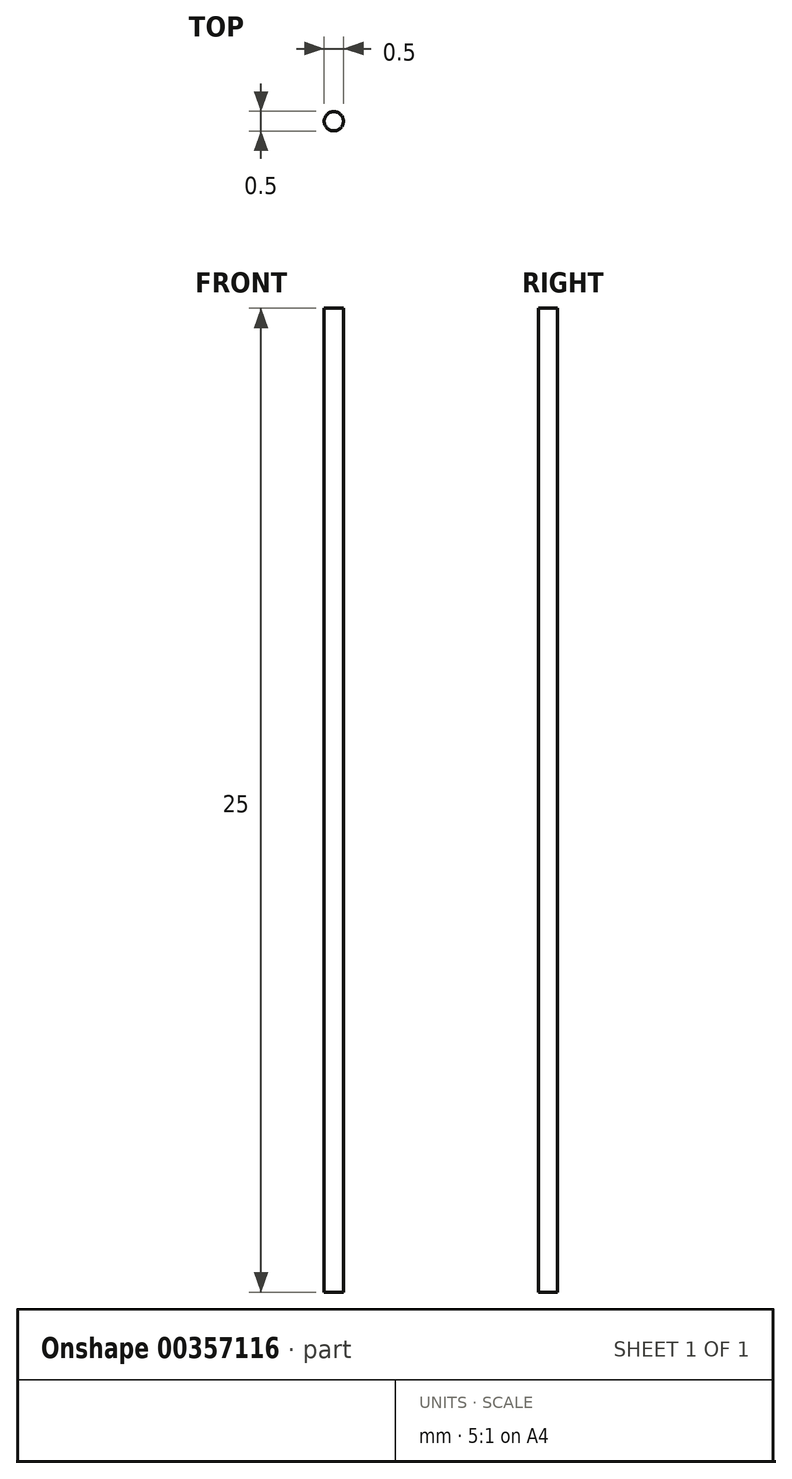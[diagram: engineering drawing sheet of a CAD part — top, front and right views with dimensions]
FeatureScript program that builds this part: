
annotation { "Feature Type Name" : "Feature", "Feature Type Description" : "" }
export const myFeature = defineFeature(function(context is Context, id is Id, definition is map)
    precondition{}
    {
        {
            var Q0;
            Q0=qCreatedBy(makeId("Top.planeOp"),FACE);
            var sketch = newSketch(context, id + "F0", { "sketchPlane" : qUnion([Q0])});
            skCircle(sketch, "E0", {"center": v(0, 0) * mm, "radius": 0.24 * mm});
            skSolve(sketch);
        }
        {
            var Q0;
            Q0=sQuery(id+"F0.wireOp",EDGE,"E0");
            extrude(context, id + "F1", {"bodyType" : ToolBodyType.SURFACE, "surfaceEntities" : qUnion([Q0]), "endBound" : BoundingType.SYMMETRIC, "depth" : 25 * mm});
        }
    });
